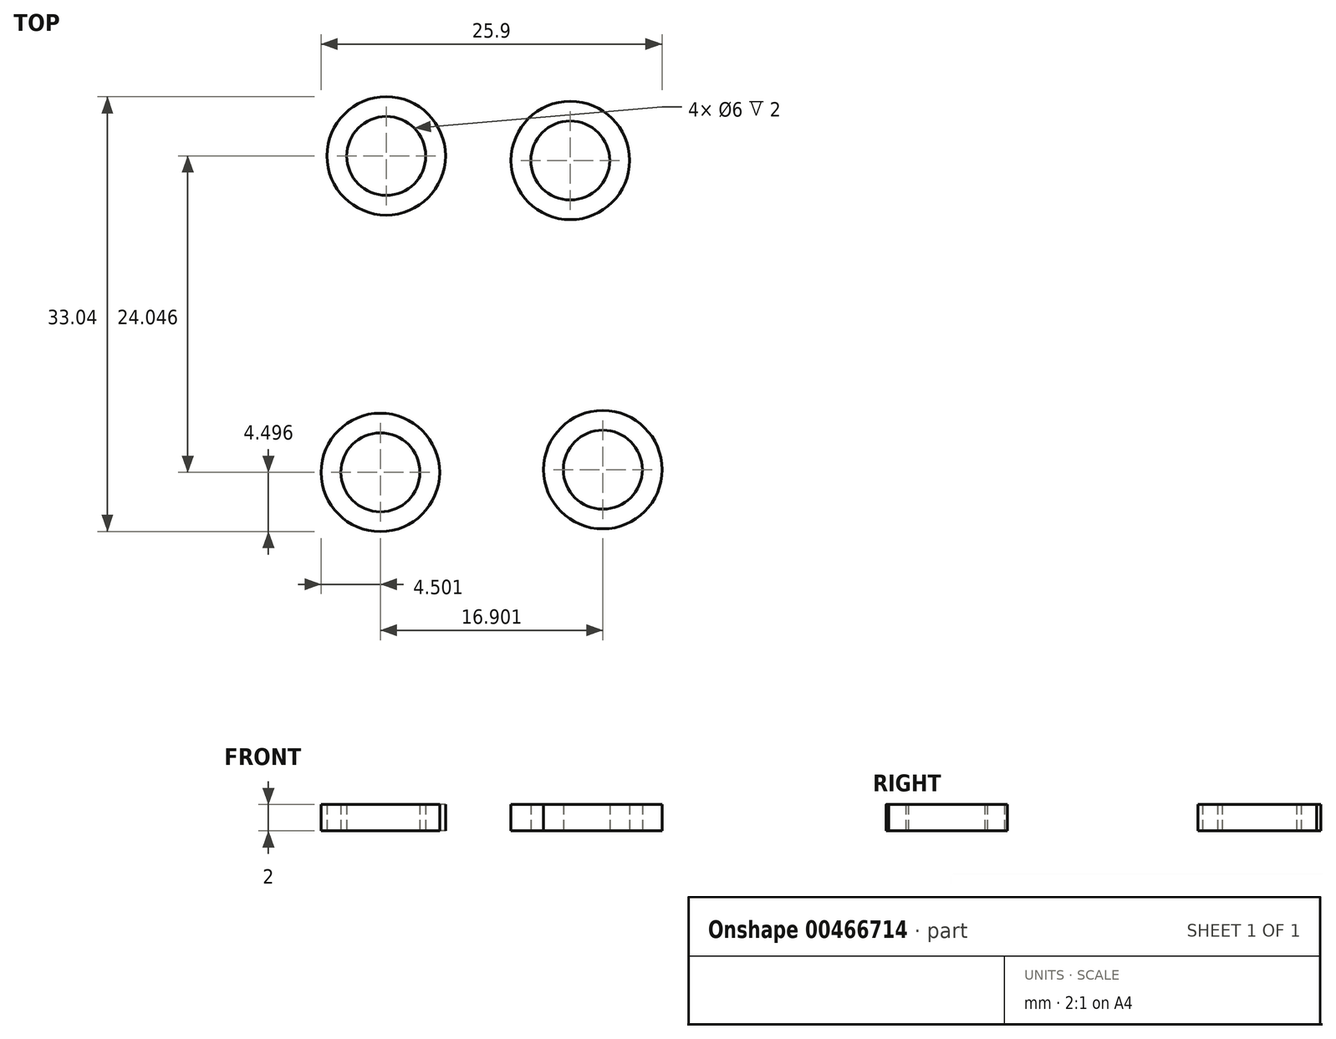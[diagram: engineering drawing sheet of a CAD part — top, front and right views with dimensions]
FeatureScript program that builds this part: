
annotation { "Feature Type Name" : "Feature", "Feature Type Description" : "" }
export const myFeature = defineFeature(function(context is Context, id is Id, definition is map)
    precondition{}
    {
        {
            var Q0;
            Q0=qCreatedBy(makeId("Top.planeOp"),FACE);
            var sketch = newSketch(context, id + "F0", { "sketchPlane" : qUnion([Q0])});
            skCircle(sketch, "E0", {"center": v(-41.97, 19.1) * mm, "radius": 4.5 * mm});
            skCircle(sketch, "E1", {"center": v(-41.97, 19.1) * mm, "radius": 3 * mm});
            skCircle(sketch, "E2", {"center": v(-42.42, -4.95) * mm, "radius": 4.5 * mm});
            skCircle(sketch, "E3", {"center": v(-42.42, -4.95) * mm, "radius": 3 * mm});
            skCircle(sketch, "E4", {"center": v(-25.52, -4.75) * mm, "radius": 4.5 * mm});
            skCircle(sketch, "E5", {"center": v(-25.52, -4.75) * mm, "radius": 3 * mm});
            skCircle(sketch, "E6", {"center": v(-28, 18.75) * mm, "radius": 4.5 * mm});
            skCircle(sketch, "E7", {"center": v(-28, 18.75) * mm, "radius": 3 * mm});
            skSolve(sketch);
        }
        {
            var Q0;
            Q0=makeQuery(id+"F0.imprint","IMPRINT",FACE,{"disambiguationData":[TD([[makeQuery(id+"F0.imprint","IMPRINT",EDGE,{"derivedFrom":sQuery(id+"F0.wireOp",EDGE,"E0")}),1.0]])]});
            var Q1;
            Q1=makeQuery(id+"F0.imprint","IMPRINT",FACE,{"disambiguationData":[TD([[makeQuery(id+"F0.imprint","IMPRINT",EDGE,{"derivedFrom":sQuery(id+"F0.wireOp",EDGE,"E6")}),1.0]])]});
            var Q2;
            Q2=makeQuery(id+"F0.imprint","IMPRINT",FACE,{"disambiguationData":[TD([[makeQuery(id+"F0.imprint","IMPRINT",EDGE,{"derivedFrom":sQuery(id+"F0.wireOp",EDGE,"E2")}),1.0]])]});
            var Q3;
            Q3=makeQuery(id+"F0.imprint","IMPRINT",FACE,{"disambiguationData":[TD([[makeQuery(id+"F0.imprint","IMPRINT",EDGE,{"derivedFrom":sQuery(id+"F0.wireOp",EDGE,"E4")}),1.0]])]});
            extrude(context, id + "F1", {"entities" : qUnion([Q0, Q1, Q2, Q3]), "depth" : 2 * mm});
        }
    });
